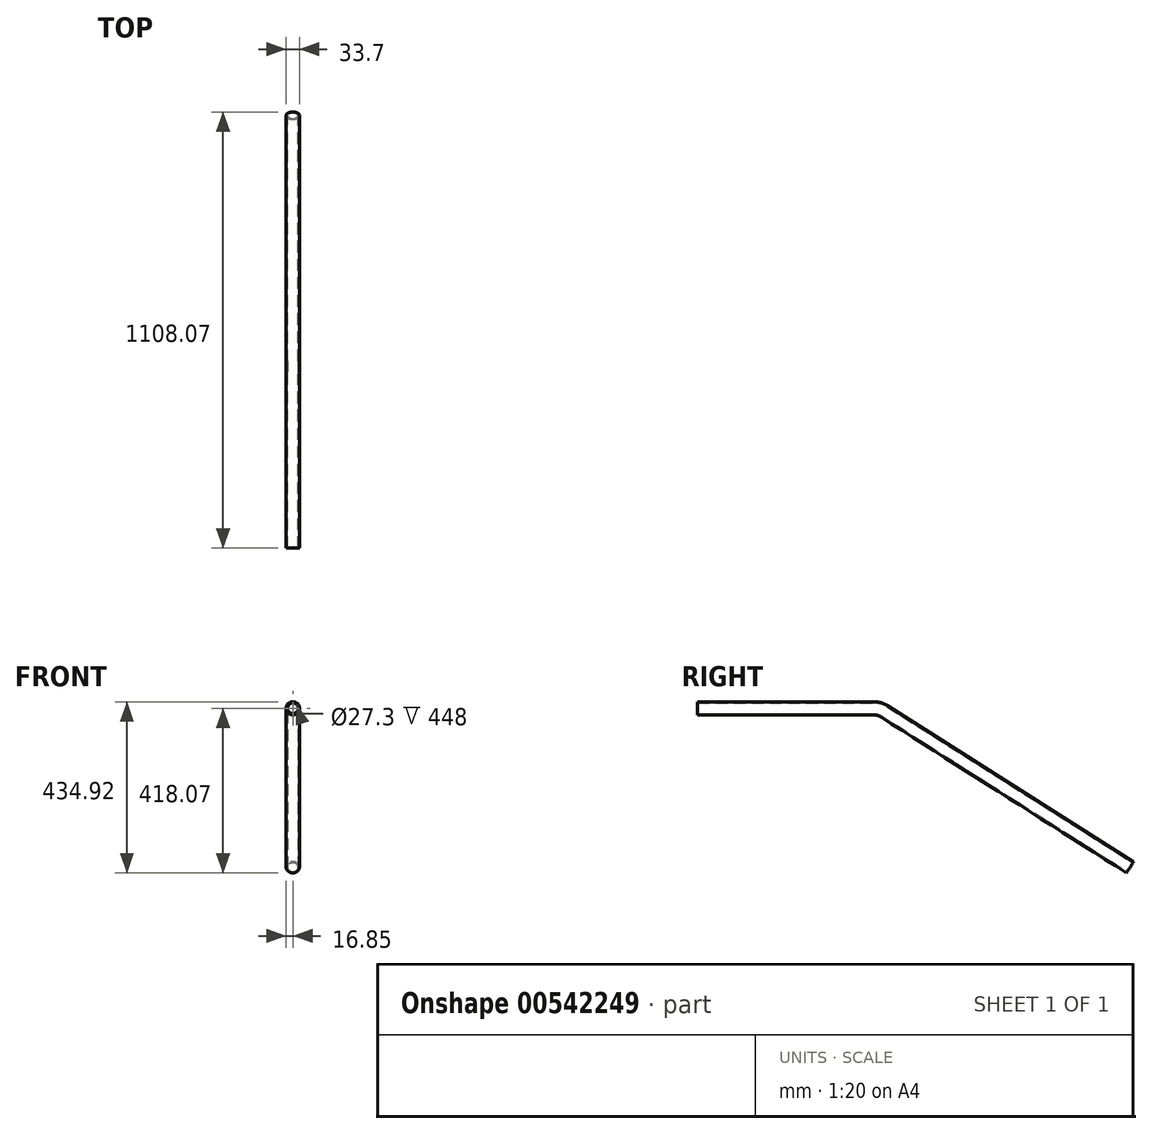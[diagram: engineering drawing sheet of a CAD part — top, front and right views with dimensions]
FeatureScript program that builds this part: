
annotation { "Feature Type Name" : "Feature", "Feature Type Description" : "" }
export const myFeature = defineFeature(function(context is Context, id is Id, definition is map)
    precondition{}
    {
        {
            var Q0;
            Q0=qCreatedBy(makeId("Right.planeOp"),FACE);
            var sketch = newSketch(context, id + "F0", { "sketchPlane" : qUnion([Q0])});
            skLineSegment(sketch, "E0", {"start": v(0, 0) * mm, "end": v(448, 0) * mm});
            skArc(sketch, "E1", {"start": v(484.11, -10.5) * mm, "mid": v(466.8, -2.68) * mm, "end": v(448, 0) * mm});
            skLineSegment(sketch, "E2", {"start": v(484.11, -10.5) * mm, "end": v(1108.07, -406.47) * mm});
            skSolve(sketch);
        }
        {
            var Q0;
            Q0=qCreatedBy(makeId("Front.planeOp"),FACE);
            var sketch = newSketch(context, id + "F1", { "sketchPlane" : qUnion([Q0])});
            skCircle(sketch, "E3", {"center": v(0, -16.85) * mm, "radius": 16.85 * mm});
            skCircle(sketch, "E4.0", {"center": v(0, -16.85) * mm, "radius": 13.65 * mm});
            skSolve(sketch);
        }
        {
            var Q0;
            Q0 = qSketchRegion(id + "F1", true);
            var Q1;
            Q1=sQuery(id+"F0.wireOp",EDGE,"E0");
            var Q2;
            Q2=sQuery(id+"F0.wireOp",EDGE,"E2");
            var Q3;
            Q3=sQuery(id+"F0.wireOp",EDGE,"E1");
            sweep(context, id + "F2", {"profiles" : qUnion([Q0]), "path" : qUnion([Q1, Q2, Q3])});
        }
    });
